# Revit family: 18-70-003 DN300
name_source: partatom
category: Pipe Accessories
units: mm (PartAtom-declared; Revit-internal decimal feet)

## family parameters
Always vertical = Yes
Cut with Voids When Loaded = No
Part Type = Valve - Breaks Into
Round Connector Dimension = Use Diameter
Shared = No
Work Plane-Based = No

## types (2) — shared parameters
1 = 1 mm  [stored 0.00328084 ft]
20 = 20 mm  [stored 0.0656168 ft]
27 = 27 mm  [stored 0.0885827 ft]
5 = 5 mm  [stored 0.0164042 ft]
50 = 50 mm  [stored 0.164042 ft]
Body_H = 370 mm  [stored 1.21391 ft]
Bore_R = 150 mm  [stored 0.492126 ft]
DN = 300 mm  [stored 0.984252 ft]
DN300_PN10 = 18-300-70-006
DN300_PN16 = 18-300-70-016
Description_ = AVK COMBI-CROSS, FLANGED, 4 OUTLETS, PN10/16
F = 14 mm  [stored 0.0459318 ft]
F1 = 20 mm  [stored 0.0656168 ft]
F2 = 65 mm  [stored 0.213255 ft]
F3 = 51 mm  [stored 0.167323 ft]
FL_R = 520 mm  [stored 1.70604 ft]
FL_T = 25 mm  [stored 0.082021 ft]
H = 740 mm  [stored 2.42782 ft]
H1 = 475 mm  [stored 1.5584 ft]
H3 = 968 mm  [stored 3.17585 ft]
H3-H = 228 mm  [stored 0.748031 ft]
L = 1050 mm  [stored 3.44488 ft]
L-L1 = 174 mm  [stored 0.570866 ft]
L1 = 702 mm  [stored 2.30315 ft]
L2 = 309 mm
L5 = 416 mm
L6 = 370 mm  [stored 1.21391 ft]
L_half = 263 mm  [stored 0.862861 ft]
OD = 260 mm  [stored 0.853018 ft]
OD1 = 143 mm
OD2 = 157 mm
P1 = 496 mm  [stored 1.6273 ft]
Raised_R = 215 mm  [stored 0.705381 ft]
Raised_dis = 4 mm  [stored 0.0131234 ft]
Search_table = 18-70-003 DN300
URL_product_pages = https://www.avkvalves.com
W = 260 mm  [stored 0.853018 ft]
arc = 370 mm  [stored 1.21391 ft]
arc1 = 108 mm
arc2 = 216 mm  [stored 0.708661 ft]
body_dim1 = 247 mm
main_dim1 = 188 mm
tp bore = 75 mm  [stored 0.246063 ft]
zero-valued in all types: Default Elevation

## per-type parameters (varying)
| type | Dh |
| DN300_PN10 | 460 mm  [stored 1.50919 ft] |
| DN300_PN16 | 470 mm  [stored 1.54199 ft] |

note: [stored X ft] marks values corroborated as IEEE doubles in the binary element streams (Revit-internal decimal feet)

## geometry (parser evidence)
native form markers: Sweep x7
no freeform markers — native parametric forms only
